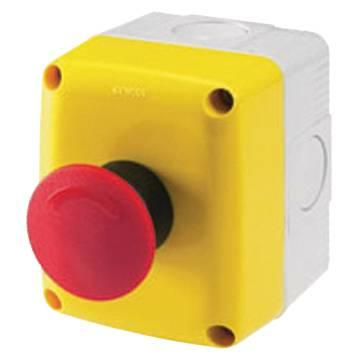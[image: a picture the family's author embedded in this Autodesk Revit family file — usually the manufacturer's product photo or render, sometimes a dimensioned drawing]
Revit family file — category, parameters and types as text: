
# Revit family: Domotics-DomesticRanges-GEWISS-27COMBI22-IP66_ENCLOSURES_1OPERATOR_D22
name_source: partatom
category: Apparecchi elettrici
revit_build: Autodesk Revit 2016 (Build: 20161004_0715(x64)
units: mm (PartAtom-declared; Revit-internal decimal feet)

## family parameters
Condiviso = No
Host = Muro
Mantenere orientamento annotazione = No
Punto di calcolo locali = No
Quota connettore circolare = Usa diametro
Sempre verticale = Sì
Taglio con vuoti quando caricato = No
Tipo di parte = Normale

## types (1)
- Domotics-DomesticRanges-GEWISS-27COMBI22-IP66_ENCLOSURES_1OPERATOR_D22
    Altezza = 120 mm  [stored 0.393701 ft]
    Catalogue = DOMOTICS
    Catalogue Range = 27COMBI
    Colour = Yellow cover
    Descrizione = ENCLOSURE 1G RED EMERGENCY BUTTON
    EAN code = 8011564055575
    Electrocod = 0212
    Glow Wire Test = 650°C
    IDF = 1d24cdab-fbde-41bc-9d64-04a2c72208b5
    IDT = 5a7eeb40-13d5-4b7f-8289-c5ccf35a1a1c
    IP degree = IP66
    Immagine tipo = GW27202.jpg
    Installation temperature = -25 +60 °C
    Insulation class = II
    Larghezza = 80 mm  [stored 0.262467 ft]
    Lid screws = Stainless steel
    Modello = GW27202
    No. gangs = 1
    Operators Ã˜ 22 = Emergency (red)
    Outer dim. LxHxD (mm) = 66x82x65
    Produttore = GEWISS S.p.A.
    Profondità = 65 mm
    Pulsante_1 = Pulsante emergenza - rosso
    SEO = Enclosure
    Scocca anteriore = Giallo
    Standard = EN 60947-1 - EN 60947-5-1
    Standard; = EN 60947-1 - EN 60947-5-1
    Technical sheet = https://www.gewiss.com
    Thermo-pressure with ball = 70
    Torque screws tightening = 0,8NM
    Type of knockout holes = Removable with tool
    URL = https://www.gewiss.com
    Version file RFA = 18.0

note: source unit labels omitted for Thermo-pressure with ball — the stored unit's dimension contradicts the parameter name (converter mislabeling)

note: [stored X ft] marks values corroborated as IEEE doubles in the binary element streams (Revit-internal decimal feet)
